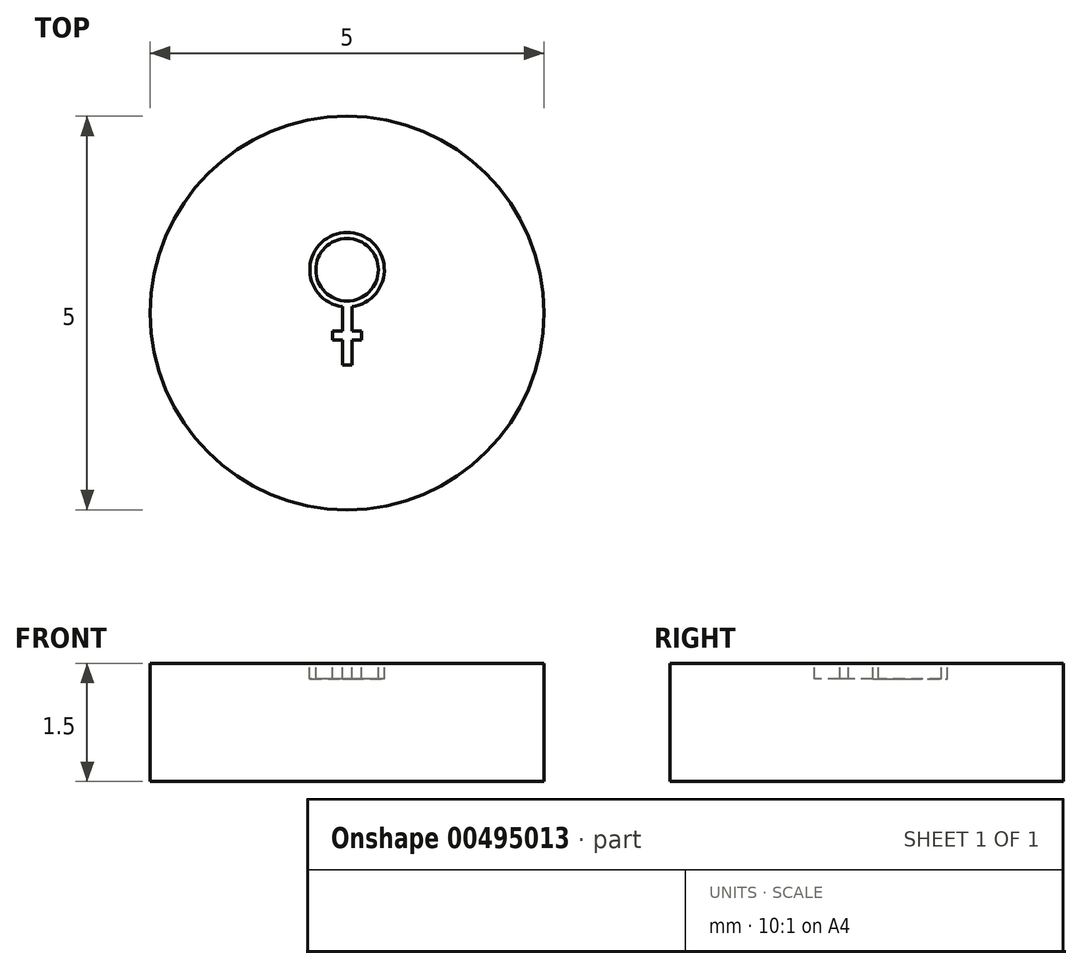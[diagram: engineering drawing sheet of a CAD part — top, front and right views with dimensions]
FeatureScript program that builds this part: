
annotation { "Feature Type Name" : "Feature", "Feature Type Description" : "" }
export const myFeature = defineFeature(function(context is Context, id is Id, definition is map)
    precondition{}
    {
        {
            var Q0;
            Q0=qCreatedBy(makeId("Top.planeOp"),FACE);
            var sketch = newSketch(context, id + "F0", { "sketchPlane" : qUnion([Q0])});
            skCircle(sketch, "E0", {"center": v(0, 0) * mm, "radius": 2.5 * mm});
            skSolve(sketch);
        }
        {
            var Q0;
            Q0=makeQuery(id+"F0.imprint","IMPRINT",FACE,{"disambiguationData":[TD([[makeQuery(id+"F0.imprint","IMPRINT",EDGE,{"derivedFrom":sQuery(id+"F0.wireOp",EDGE,"E0")}),1.0]])]});
            extrude(context, id + "F1", {"entities" : qUnion([Q0]), "depth" : 1.5 * mm, "offsetDistance" : 25.4 * mm});
        }
        {
            var Q0;
            Q0=makeQuery(id+"F1.opExtrude","CAP_FACE",FACE,{"disambiguationData":[OSD([sQuery(id+"F0.wireOp",EDGE,"E0")])],"isStart":false});
            var sketch = newSketch(context, id + "F2", { "sketchPlane" : qUnion([Q0])});
            skCircle(sketch, "E1", {"center": v(0, 0.55) * mm, "radius": 0.4 * mm});
            skArc(sketch, "E2", {"start": v(0.06, 0.08) * mm, "mid": v(0, 1.02) * mm, "end": v(-0.06, 0.08) * mm});
            skLineSegment(sketch, "E3", {"start": v(-0.06, 0.08) * mm, "end": v(-0.06, -0.23) * mm});
            skLineSegment(sketch, "E4", {"start": v(-0.06, -0.23) * mm, "end": v(-0.18, -0.23) * mm});
            skLineSegment(sketch, "E5", {"start": v(-0.18, -0.23) * mm, "end": v(-0.18, -0.34) * mm});
            skLineSegment(sketch, "E6", {"start": v(-0.18, -0.34) * mm, "end": v(-0.06, -0.34) * mm});
            skLineSegment(sketch, "E7", {"start": v(-0.06, -0.34) * mm, "end": v(-0.06, -0.66) * mm});
            skLineSegment(sketch, "E8", {"start": v(-0.06, -0.66) * mm, "end": v(0, -0.66) * mm});
            skLineSegment(sketch, "E9.MirrorCS", {"start": v(0.06, 0.08) * mm, "end": v(0.06, -0.23) * mm});
            skLineSegment(sketch, "E10.MirrorCS", {"start": v(0.06, -0.23) * mm, "end": v(0.18, -0.23) * mm});
            skLineSegment(sketch, "E11.MirrorCS", {"start": v(0.18, -0.23) * mm, "end": v(0.18, -0.34) * mm});
            skLineSegment(sketch, "E12.MirrorCS", {"start": v(0.18, -0.34) * mm, "end": v(0.06, -0.34) * mm});
            skLineSegment(sketch, "E13.MirrorCS", {"start": v(0.06, -0.34) * mm, "end": v(0.06, -0.66) * mm});
            skLineSegment(sketch, "E14.MirrorCS", {"start": v(0.06, -0.66) * mm, "end": v(0, -0.66) * mm});
            skSolve(sketch);
        }
        {
            var Q0;
            Q0=makeQuery(id+"F2.imprint","IMPRINT",FACE,{"disambiguationData":[TD([[makeQuery(id+"F2.imprint","IMPRINT",EDGE,{"derivedFrom":sQuery(id+"F2.wireOp",EDGE,"E1")}),-1.0]])]});
            extrude(context, id + "F3", {"entities" : qUnion([Q0]), "operationType" : NewBodyOperationType.REMOVE, "oppositeDirection" : true, "depth" : .2 * mm, "offsetDistance" : 25.4 * mm});
        }
    });
